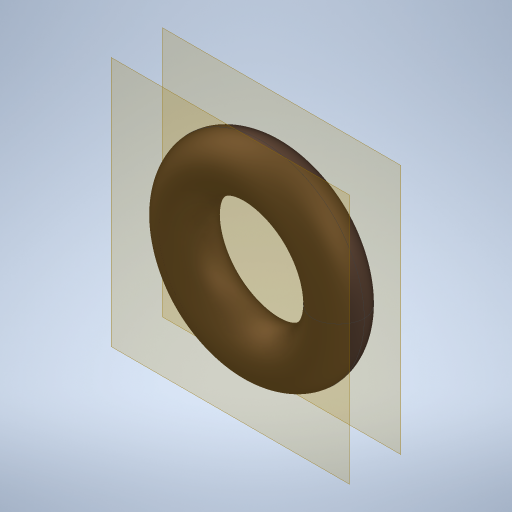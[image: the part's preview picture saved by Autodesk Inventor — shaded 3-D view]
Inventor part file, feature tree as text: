
AUTODESK INVENTOR PART (.ipt)
format: ipt  version: 2024 (Build 280153000, 153)  size: 323,584 bytes
history: native  units: in
note: dims shown in document units (in); Inventor stores cm internally (conversion verified against a paired STEP export)
features: other x3, plane x2
ambient origin geometry x8: Origin, YZ Plane, XZ Plane, XY Plane, X Axis, Y Axis, Z Axis, Center Point
bodies: Solid1 (feature_tree)
feature tree (5):
  other  "SA O-Ring.ipt"
  other  "Solid1::SA O-Ring.ipt"
  other  "TaggingFeature1"
  plane  "Work Plane1"
  plane  "Work Plane2"
